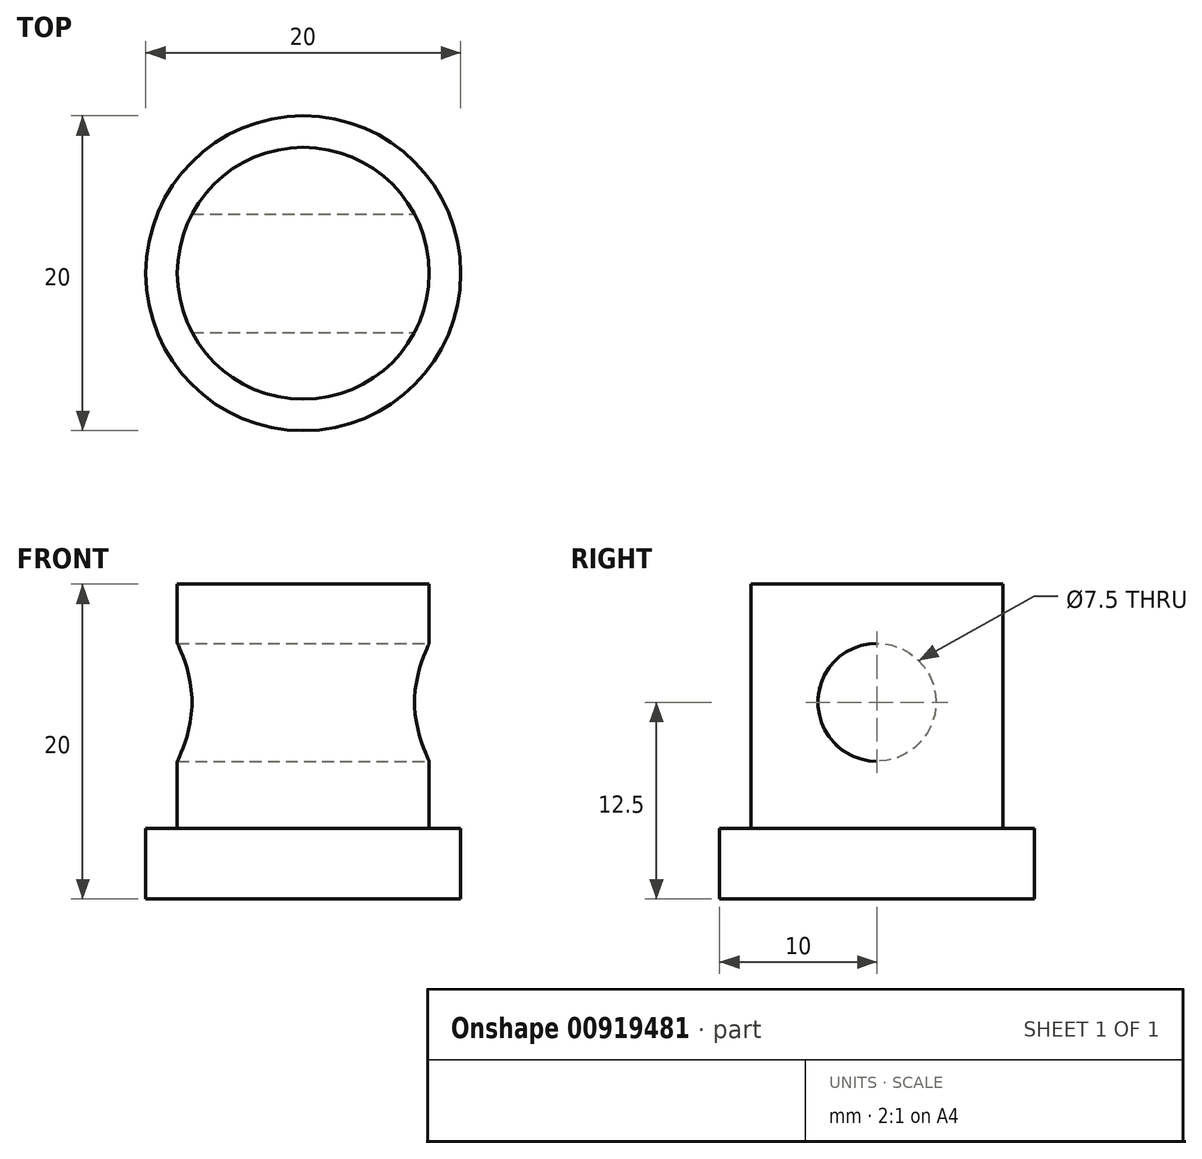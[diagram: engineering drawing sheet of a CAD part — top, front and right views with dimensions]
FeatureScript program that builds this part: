
annotation { "Feature Type Name" : "Feature", "Feature Type Description" : "" }
export const myFeature = defineFeature(function(context is Context, id is Id, definition is map)
    precondition{}
    {
        {
            var Q0;
            Q0=qCreatedBy(makeId("Top.planeOp"),FACE);
            var sketch = newSketch(context, id + "F0", { "sketchPlane" : qUnion([Q0])});
            skCircle(sketch, "E0", {"center": v(0, 0) * mm, "radius": 10 * mm});
            skSolve(sketch);
        }
        {
            var Q0;
            Q0=makeQuery(id+"F0.imprint","IMPRINT",FACE,{"disambiguationData":[TD([[makeQuery(id+"F0.imprint","IMPRINT",EDGE,{"derivedFrom":sQuery(id+"F0.wireOp",EDGE,"E0")}),1.0]])]});
            extrude(context, id + "F1", {"entities" : qUnion([Q0]), "depth" : 20 * mm, "offsetDistance" : 25 * mm});
        }
        {
            var Q0;
            Q0=makeQuery(id+"F1.opExtrude","CAP_FACE",FACE,{"disambiguationData":[OSD([sQuery(id+"F0.wireOp",EDGE,"E0")])],"isStart":false});
            var sketch = newSketch(context, id + "F2", { "sketchPlane" : qUnion([Q0])});
            skCircle(sketch, "E1", {"center": v(0, 0) * mm, "radius": 10 * mm});
            skCircle(sketch, "E2.0", {"center": v(0, 0) * mm, "radius": 8 * mm});
            skSolve(sketch);
        }
        {
            var Q0;
            Q0=qSketchRegion(id+"F2",true);
            extrude(context, id + "F3", {"entities" : qUnion([Q0]), "operationType" : NewBodyOperationType.REMOVE, "oppositeDirection" : true, "depth" : 15.5 * mm, "offsetDistance" : 25 * mm});
        }
        {
            var Q0;
            Q0=qCreatedBy(makeId("Right.planeOp"),FACE);
            cPlane(context, id + "F4", {"entities" : qUnion([Q0]), "cplaneType" : CPlaneType.OFFSET, "offset" : 10 * mm, "width" : 150 * mm, "height" : 150 * mm});
        }
        {
            var Q0;
            Q0=qCreatedBy(id+"F4.planeOp",FACE);
            var sketch = newSketch(context, id + "F5", { "sketchPlane" : qUnion([Q0])});
            skCircle(sketch, "E3", {"center": v(0, 12.5) * mm, "radius": 3.75 * mm});
            skSolve(sketch);
        }
        {
            var Q0;
            Q0 = qSketchRegion(id + "F5", true);
            extrude(context, id + "F6", {"entities" : qUnion([Q0]), "operationType" : NewBodyOperationType.REMOVE, "oppositeDirection" : true, "depth" : 25 * mm, "offsetDistance" : 25 * mm});
        }
    });
